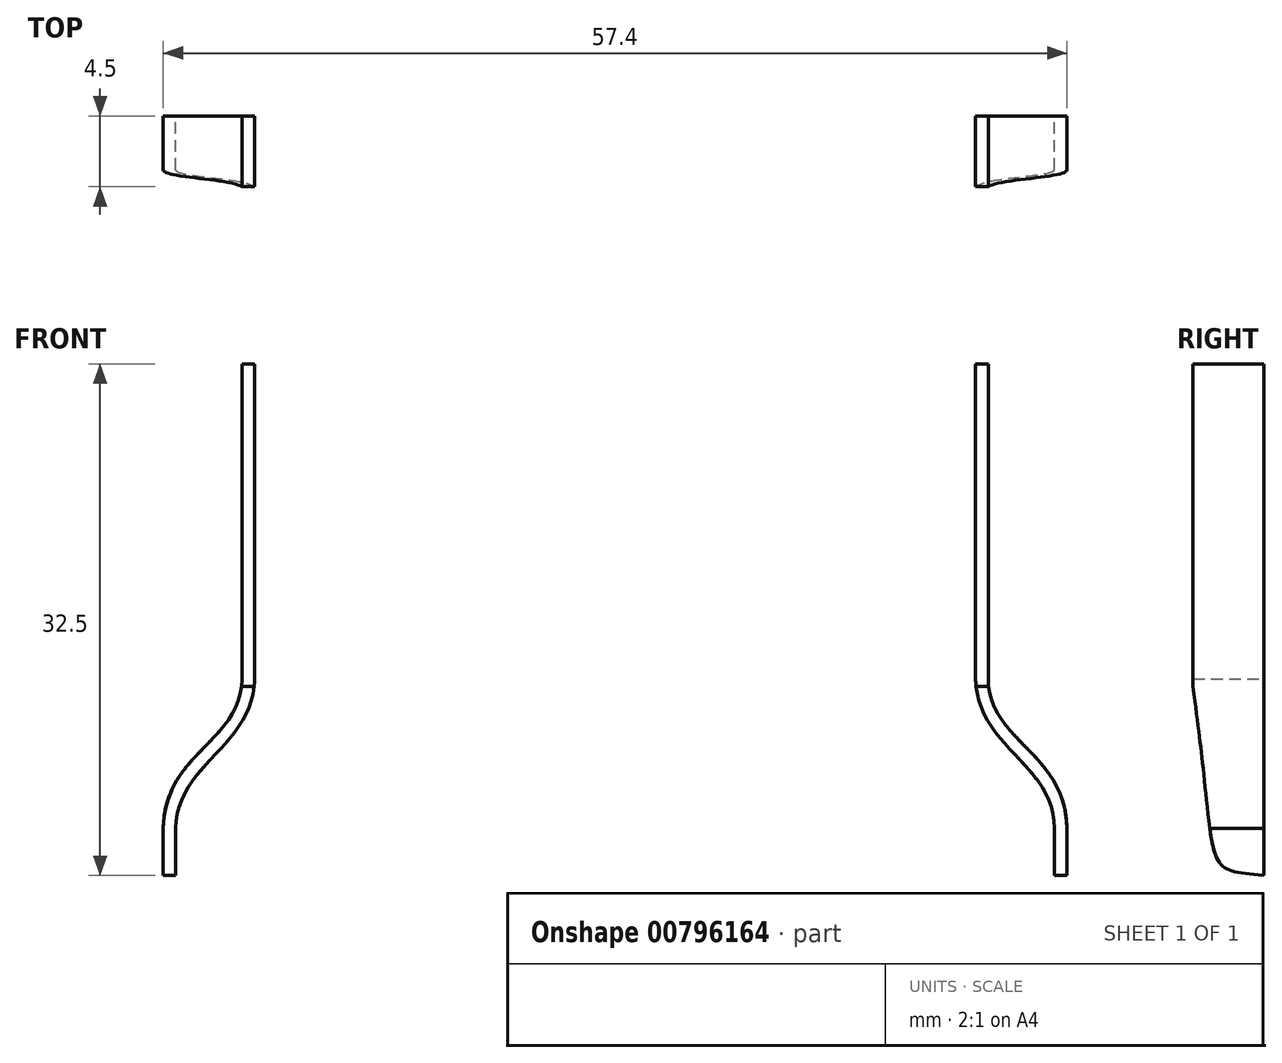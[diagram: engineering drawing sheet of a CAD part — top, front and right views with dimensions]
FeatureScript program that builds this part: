
annotation { "Feature Type Name" : "Feature", "Feature Type Description" : "" }
export const myFeature = defineFeature(function(context is Context, id is Id, definition is map)
    precondition{}
    {
        {
            var Q0;
            Q0=qCreatedBy(makeId("Front.planeOp"),FACE);
            var sketch = newSketch(context, id + "F0", { "sketchPlane" : qUnion([Q0])});
            skLineSegment(sketch, "E0", {"start": v(2.1, 32.5) * mm, "end": v(2.1, 12.5) * mm});
            skLineSegment(sketch, "E1", {"start": v(-2.9, 3) * mm, "end": v(-2.9, 0) * mm});
            skFitSpline(sketch, "E2", {"points": [v(2.1, 12.5) * mm, v(-2.9, 3) * mm], "startDerivative": vector(-0.18, -12.96) * mm, "endDerivative": vector(-0.06, -12.34) * mm});
            skLineSegment(sketch, "E3", {"start": v(1.3, 32.5) * mm, "end": v(1.3, 12.5) * mm});
            skLineSegment(sketch, "E4", {"start": v(-3.7, 3) * mm, "end": v(-3.7, 0) * mm});
            skFitSpline(sketch, "E5", {"points": [v(1.3, 12.5) * mm, v(-3.7, 3) * mm], "startDerivative": vector(0.01, -11.83) * mm, "endDerivative": vector(-0.23, -14.42) * mm});
            skLineSegment(sketch, "E6", {"start": v(1.3, 32.5) * mm, "end": v(2.1, 32.5) * mm});
            skLineSegment(sketch, "E7", {"start": v(-3.7, 0) * mm, "end": v(-2.9, 0) * mm});
            skPoint(sketch, "E8.visualSharp", {"position": v(-3.7, 0) * mm});
            skLineSegment(sketch, "E8.filletArc", {"start": v(-3.7, 0) * mm, "end": v(-3.7, 0) * mm});
            skPoint(sketch, "E9.visualSharp", {"position": v(-2.9, 0) * mm});
            skLineSegment(sketch, "E9.filletArc", {"start": v(-2.9, 0) * mm, "end": v(-2.9, 0) * mm});
            skSolve(sketch);
        }
        {
            var Q0;
            Q0=makeQuery(id+"F0.imprint","IMPRINT",FACE,{"disambiguationData":[TD([[makeQuery(id+"F0.imprint","IMPRINT",EDGE,{"derivedFrom":sQuery(id+"F0.wireOp",EDGE,"E0")}),-1.0]])]});
            extrude(context, id + "F1", {"entities" : qUnion([Q0]), "depth" : 50 * mm, "offsetDistance" : 25 * mm});
        }
        {
            var Q0;
            Q0=qCreatedBy(makeId("Right.planeOp"),FACE);
            cPlane(context, id + "F2", {"entities" : qUnion([Q0]), "cplaneType" : CPlaneType.OFFSET, "offset" : 25 * mm, "width" : 150 * mm, "height" : 150 * mm});
        }
        {
            var Q0;
            Q0=qCreatedBy(id+"F2.planeOp",FACE);
            var sketch = newSketch(context, id + "F3", { "sketchPlane" : qUnion([Q0])});
            skLineSegment(sketch, "E10", {"start": v(-4.5, 32.5) * mm, "end": v(-4.5, 12) * mm});
            skLineSegment(sketch, "E11", {"start": v(-4.5, 32.5) * mm, "end": v(0, 32.5) * mm});
            skLineSegment(sketch, "E12", {"start": v(0, 32.5) * mm, "end": v(0, 0) * mm});
            skFitSpline(sketch, "E13", {"points": [v(-4.5, 12) * mm, v(0, 0) * mm], "startDerivative": vector(5.06, -36) * mm, "endDerivative": vector(12.48, -1.26) * mm});
            skSolve(sketch);
        }
        {
            var Q0;
            Q0=makeQuery(id+"F3.imprint","IMPRINT",FACE,{"disambiguationData":[TD([[makeQuery(id+"F3.imprint","IMPRINT",EDGE,{"derivedFrom":sQuery(id+"F3.wireOp",EDGE,"E10")}),1.0]])]});
            extrude(context, id + "F4", {"entities" : qUnion([Q0]), "operationType" : NewBodyOperationType.INTERSECT, "endBound" : BoundingType.SYMMETRIC, "depth" : 70 * mm, "offsetDistance" : 25 * mm});
        }
        {
            var Q0;
            Q0=makeQuery(id+"F1.opExtrude","SWEPT_BODY",BODY,{"disambiguationData":[OSD([sQuery(id+"F0.wireOp",EDGE,"E0"),sQuery(id+"F0.wireOp",EDGE,"E1"),sQuery(id+"F0.wireOp",EDGE,"E2"),sQuery(id+"F0.wireOp",EDGE,"E3"),sQuery(id+"F0.wireOp",EDGE,"E4"),sQuery(id+"F0.wireOp",EDGE,"E5"),sQuery(id+"F0.wireOp",EDGE,"E6"),sQuery(id+"F0.wireOp",EDGE,"E7")])]});
            var Q1;
            Q1=qCreatedBy(id+"F2.planeOp",FACE);
            mirror(context, id + "F5", {"entities" : qUnion([Q0]), "mirrorPlane" : qUnion([Q1])});
        }
    });
